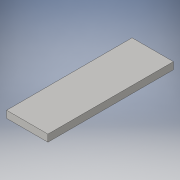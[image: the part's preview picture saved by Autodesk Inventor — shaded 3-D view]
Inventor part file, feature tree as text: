
AUTODESK INVENTOR PART (.ipt)
format: ipt  version: 2016 (Build 200138000, 138)  size: 86,016 bytes
history: native  units: in
note: dims shown in document units (in); Inventor stores cm internally (conversion verified against a paired STEP export)
features: extrude x1, sketch x1
ambient origin geometry x8: Origin, YZ Plane, XZ Plane, XY Plane, X Axis, Y Axis, Z Axis, Center Point
bodies: Solid1 (feature_tree)
feature tree (2):
  extrude  "Extrusion1"  Depth=6.6in
  sketch  "Sketch1"  dims[d0=2.174in d1=6.6in d2=0.3701in d3=0.0in]
